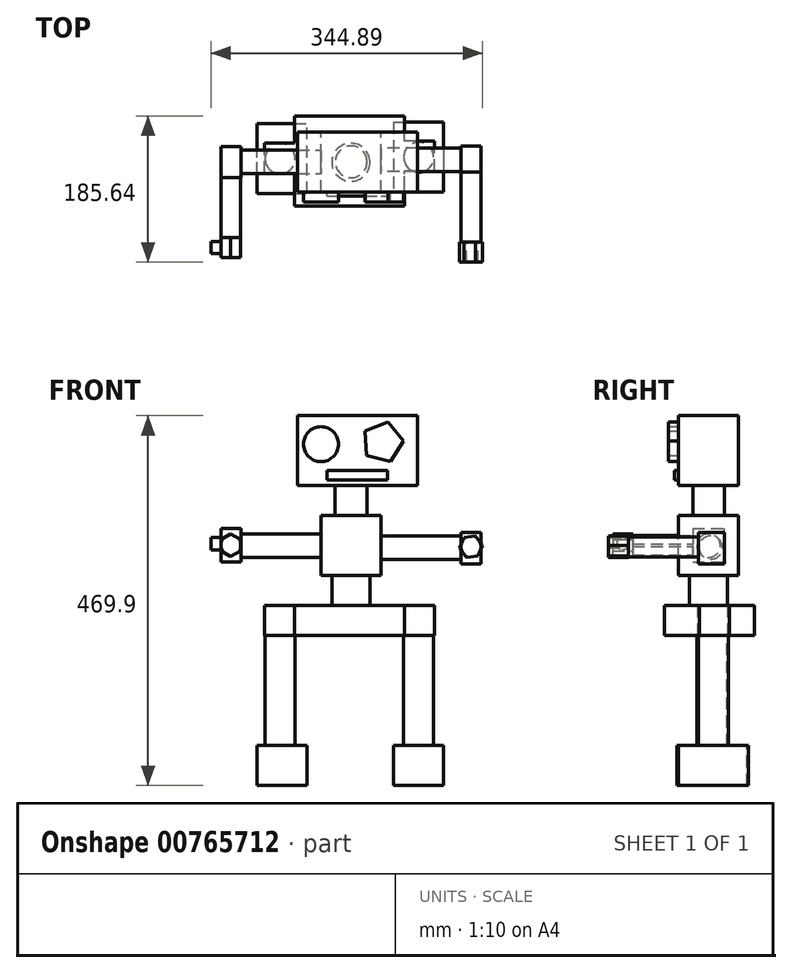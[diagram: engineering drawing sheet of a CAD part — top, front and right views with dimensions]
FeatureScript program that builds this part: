
annotation { "Feature Type Name" : "Feature", "Feature Type Description" : "" }
export const myFeature = defineFeature(function(context is Context, id is Id, definition is map)
    precondition{}
    {
        {
            var Q0;
            Q0=qCreatedBy(makeId("Front.planeOp"),FACE);
            var sketch = newSketch(context, id + "F0", { "sketchPlane" : qUnion([Q0])});
            skLineSegment(sketch, "E0.bottom", {"start": v(0, 0) * mm, "end": v(76.2, 0) * mm});
            skLineSegment(sketch, "E0.top", {"start": v(0, 76.2) * mm, "end": v(76.2, 76.2) * mm});
            skLineSegment(sketch, "E0.left", {"start": v(0, 0) * mm, "end": v(0, 76.2) * mm});
            skLineSegment(sketch, "E0.right", {"start": v(76.2, 0) * mm, "end": v(76.2, 76.2) * mm});
            skSolve(sketch);
        }
        {
            var Q0;
            Q0=makeQuery(id+"F0.imprint","IMPRINT",FACE,{"disambiguationData":[TD([[makeQuery(id+"F0.imprint","IMPRINT",EDGE,{"derivedFrom":sQuery(id+"F0.wireOp",EDGE,"E0.bottom")}),1.0]])]});
            extrude(context, id + "F1", {"entities" : qUnion([Q0]), "depth" : 76.2 * mm, "offsetDistance" : 25.4 * mm});
        }
        {
            var Q0;
            Q0=makeQuery(id+"F1.opExtrude","SWEPT_FACE",FACE,{"disambiguationData":[OSD([sQuery(id+"F0.wireOp",EDGE,"E0.bottom")])]});
            var sketch = newSketch(context, id + "F2", { "sketchPlane" : qUnion([Q0])});
            skPoint(sketch, "E1", {"position": v(38.1, 38.1) * mm});
            skSolve(sketch);
        }
        {
            var Q0;
            Q0=makeQuery(id+"F1.opExtrude","SWEPT_FACE",FACE,{"disambiguationData":[OSD([sQuery(id+"F0.wireOp",EDGE,"E0.right")])]});
            var sketch = newSketch(context, id + "F3", { "sketchPlane" : qUnion([Q0])});
            skCircle(sketch, "E2", {"center": v(-35.37, 35.61) * mm, "radius": 14.83 * mm});
            skSolve(sketch);
        }
        {
            var Q0;
            Q0 = qSketchRegion(id + "F3", true);
            extrude(context, id + "F4", {"entities" : qUnion([Q0]), "operationType" : NewBodyOperationType.ADD, "depth" : 101.6 * mm, "offsetDistance" : 25.4 * mm});
        }
        {
            var Q0;
            Q0=makeQuery(id+"F4.opExtrude","CAP_FACE",FACE,{"disambiguationData":[OSD([sQuery(id+"F3.wireOp",EDGE,"E2")])],"isStart":false});
            var sketch = newSketch(context, id + "F5", { "sketchPlane" : qUnion([Q0])});
            skLineSegment(sketch, "E3.bottom", {"start": v(-18.2, 54.98) * mm, "end": v(-51.02, 54.98) * mm});
            skLineSegment(sketch, "E3.top", {"start": v(-18.2, 14.56) * mm, "end": v(-51.02, 14.56) * mm});
            skLineSegment(sketch, "E3.left", {"start": v(-18.2, 54.98) * mm, "end": v(-18.2, 14.56) * mm});
            skLineSegment(sketch, "E3.right", {"start": v(-51.02, 54.98) * mm, "end": v(-51.02, 14.56) * mm});
            skSolve(sketch);
        }
        {
            var Q0;
            Q0 = qSketchRegion(id + "F5", true);
            extrude(context, id + "F6", {"entities" : qUnion([Q0]), "operationType" : NewBodyOperationType.ADD, "depth" : 25.4 * mm, "offsetDistance" : 25.4 * mm});
        }
        {
            var Q0;
            Q0=makeQuery(id+"F6.opExtrude","SWEPT_FACE",FACE,{"disambiguationData":[OSD([sQuery(id+"F5.wireOp",EDGE,"E3.right")])]});
            var sketch = newSketch(context, id + "F7", { "sketchPlane" : qUnion([Q0])});
            skCircle(sketch, "E4", {"center": v(190.5, 36.6) * mm, "radius": 12.7 * mm});
            skPoint(sketch, "E4.centerSnap0", {"position": v(190.5, 14.56) * mm});
            skSolve(sketch);
        }
        {
            var Q0;
            Q0 = qSketchRegion(id + "F7", true);
            extrude(context, id + "F8", {"entities" : qUnion([Q0]), "operationType" : NewBodyOperationType.ADD, "depth" : 88.9 * mm, "offsetDistance" : 25.4 * mm});
        }
        {
            var Q0;
            Q0=makeQuery(id+"F1.opExtrude","SWEPT_FACE",FACE,{"disambiguationData":[OSD([sQuery(id+"F0.wireOp",EDGE,"E0.left")])]});
            var sketch = newSketch(context, id + "F9", { "sketchPlane" : qUnion([Q0])});
            skPoint(sketch, "E5", {"position": v(38.1, 38.1) * mm});
            skPoint(sketch, "E5.positionSnap0", {"position": v(0, 38.1) * mm});
            skSolve(sketch);
        }
        {
            var Q0;
            {var subQ0=sQuery(id+"F0.wireOp",EDGE,"E0.left");Q0=makeQuery(id+"F9.imprint","IMPRINT",FACE,{"disambiguationData":[TD([[makeQuery(id+"F9.imprint","IMPRINT",EDGE,{"derivedFrom":makeQuery(id+"F1.opExtrude","CAP_EDGE",EDGE,{"disambiguationData":[OSD([subQ0])],"isStart":true})}),-1.0]])]});}
            var sketch = newSketch(context, id + "F10", { "sketchPlane" : qUnion([Q0])});
            skCircle(sketch, "E6", {"center": v(38.01, 38.14) * mm, "radius": 14.96 * mm});
            skSolve(sketch);
        }
        {
            var Q0;
            Q0 = qSketchRegion(id + "F10", true);
            extrude(context, id + "F11", {"entities" : qUnion([Q0]), "operationType" : NewBodyOperationType.ADD, "depth" : 101.6 * mm, "offsetDistance" : 25.4 * mm});
        }
        {
            var Q0;
            Q0=makeQuery(id+"F11.opExtrude","CAP_FACE",FACE,{"disambiguationData":[OSD([sQuery(id+"F10.wireOp",EDGE,"E6")])],"isStart":false});
            var sketch = newSketch(context, id + "F12", { "sketchPlane" : qUnion([Q0])});
            skLineSegment(sketch, "E7.bottom", {"start": v(58.05, 59.82) * mm, "end": v(18.68, 59.82) * mm});
            skLineSegment(sketch, "E7.top", {"start": v(58.05, 17.57) * mm, "end": v(18.68, 17.57) * mm});
            skLineSegment(sketch, "E7.left", {"start": v(58.05, 59.82) * mm, "end": v(58.05, 17.57) * mm});
            skLineSegment(sketch, "E7.right", {"start": v(18.68, 59.82) * mm, "end": v(18.68, 17.57) * mm});
            skSolve(sketch);
        }
        {
            var Q0;
            Q0 = qSketchRegion(id + "F12", true);
            extrude(context, id + "F13", {"entities" : qUnion([Q0]), "operationType" : NewBodyOperationType.ADD, "depth" : 25.4 * mm, "offsetDistance" : 25.4 * mm});
        }
        {
            var Q0;
            Q0=makeQuery(id+"F13.opExtrude","SWEPT_FACE",FACE,{"disambiguationData":[OSD([sQuery(id+"F12.wireOp",EDGE,"E7.left")])]});
            var sketch = newSketch(context, id + "F14", { "sketchPlane" : qUnion([Q0])});
            skCircle(sketch, "E8", {"center": v(-114.67, 38.58) * mm, "radius": 12.46 * mm});
            skSolve(sketch);
        }
        {
            var Q0;
            {var subQ0=sQuery(id+"F14.wireOp",EDGE,"E8");var subQ1=makeQuery(id+"F13.opExtrude","CAP_EDGE",EDGE,{"disambiguationData":[OSD([sQuery(id+"F12.wireOp",EDGE,"E7.left")])],"isStart":false});var subQ2=makeQuery(id+"F14.imprint","INTERSECT",VERTEX,{"disambiguationData":[OD(0.0)],"derivedFrom":[subQ1,subQ0]});Q0=makeQuery(id+"F14.imprint","IMPRINT",FACE,{"disambiguationData":[TD([[makeQuery(id+"F14.imprint","IMPRINT",EDGE,{"disambiguationData":[TD([[subQ2,1.0]])],"derivedFrom":subQ0}),1.0]])]});}
            extrude(context, id + "F15", {"entities" : qUnion([Q0]), "operationType" : NewBodyOperationType.ADD, "depth" : 76.2 * mm, "offsetDistance" : 25.4 * mm});
        }
        {
            var Q0;
            Q0=makeQuery(id+"F15.opExtrude","CAP_FACE",FACE,{"disambiguationData":[OSD([sQuery(id+"F14.wireOp",EDGE,"E8")])],"isStart":false});
            var sketch = newSketch(context, id + "F16", { "sketchPlane" : qUnion([Q0])});
            skCircle(sketch, "E9.cCircle", {"center": v(-114.67, 38.58) * mm, "radius": 12.46 * mm, "construction": true});
            skLineSegment(sketch, "E9.0", {"start": v(-102.2, 45.77) * mm, "end": v(-102.2, 31.38) * mm});
            skLineSegment(sketch, "E9.1", {"start": v(-102.2, 31.38) * mm, "end": v(-114.67, 24.18) * mm});
            skLineSegment(sketch, "E9.2", {"start": v(-114.67, 24.18) * mm, "end": v(-127.13, 31.38) * mm});
            skLineSegment(sketch, "E9.3", {"start": v(-127.13, 31.38) * mm, "end": v(-127.13, 45.77) * mm});
            skLineSegment(sketch, "E9.4", {"start": v(-127.13, 45.77) * mm, "end": v(-114.67, 52.97) * mm});
            skLineSegment(sketch, "E9.5", {"start": v(-114.67, 52.97) * mm, "end": v(-102.2, 45.77) * mm});
            skPoint(sketch, "E9.0.midPoint", {"position": v(-102.2, 38.58) * mm});
            skSolve(sketch);
        }
        {
            var Q0;
            Q0 = qSketchRegion(id + "F16", true);
            extrude(context, id + "F17", {"entities" : qUnion([Q0]), "operationType" : NewBodyOperationType.ADD, "depth" : 25.4 * mm, "offsetDistance" : 25.4 * mm});
        }
        {
            var Q0;
            Q0=makeQuery(id+"F8.opExtrude","CAP_FACE",FACE,{"disambiguationData":[OSD([sQuery(id+"F7.wireOp",EDGE,"E4")])],"isStart":false});
            var sketch = newSketch(context, id + "F18", { "sketchPlane" : qUnion([Q0])});
            skCircle(sketch, "E10.cCircle", {"center": v(190.5, 36.6) * mm, "radius": 12.7 * mm, "construction": true});
            skLineSegment(sketch, "E10.0", {"start": v(205.06, 38.37) * mm, "end": v(199.31, 24.88) * mm});
            skLineSegment(sketch, "E10.1", {"start": v(199.31, 24.88) * mm, "end": v(184.75, 23.11) * mm});
            skLineSegment(sketch, "E10.2", {"start": v(184.75, 23.11) * mm, "end": v(175.94, 34.83) * mm});
            skLineSegment(sketch, "E10.3", {"start": v(175.94, 34.83) * mm, "end": v(181.69, 48.33) * mm});
            skLineSegment(sketch, "E10.4", {"start": v(181.69, 48.33) * mm, "end": v(196.25, 50.1) * mm});
            skLineSegment(sketch, "E10.5", {"start": v(196.25, 50.1) * mm, "end": v(205.06, 38.37) * mm});
            skPoint(sketch, "E10.0.midPoint", {"position": v(202.18, 31.63) * mm});
            skSolve(sketch);
        }
        {
            var Q0;
            Q0 = qSketchRegion(id + "F18", true);
            extrude(context, id + "F19", {"entities" : qUnion([Q0]), "operationType" : NewBodyOperationType.ADD, "depth" : 25.4 * mm, "offsetDistance" : 25.4 * mm});
        }
        {
            var Q0;
            {var subQ0=sQuery(id+"F0.wireOp",EDGE,"E0.bottom");Q0=makeQuery(id+"F2.imprint","IMPRINT",FACE,{"disambiguationData":[TD([[makeQuery(id+"F2.imprint","IMPRINT",EDGE,{"derivedFrom":makeQuery(id+"F1.opExtrude","CAP_EDGE",EDGE,{"disambiguationData":[OSD([subQ0])],"isStart":true})}),1.0]])]});}
            var sketch = newSketch(context, id + "F20", { "sketchPlane" : qUnion([Q0])});
            skCircle(sketch, "E11", {"center": v(37.98, 38.47) * mm, "radius": 24.15 * mm});
            skSolve(sketch);
        }
        {
            var Q0;
            Q0 = qSketchRegion(id + "F20", true);
            extrude(context, id + "F21", {"entities" : qUnion([Q0]), "operationType" : NewBodyOperationType.ADD, "depth" : 38.1 * mm, "offsetDistance" : 25.4 * mm});
        }
        {
            var Q0;
            Q0=makeQuery(id+"F21.opExtrude","CAP_FACE",FACE,{"disambiguationData":[OSD([sQuery(id+"F20.wireOp",EDGE,"E11")])],"isStart":false});
            var sketch = newSketch(context, id + "F22", { "sketchPlane" : qUnion([Q0])});
            skLineSegment(sketch, "E12.bottom", {"start": v(-33.76, 93.98) * mm, "end": v(105.94, 93.98) * mm});
            skLineSegment(sketch, "E12.top", {"start": v(-33.76, -20.32) * mm, "end": v(105.94, -20.32) * mm});
            skLineSegment(sketch, "E12.left", {"start": v(-33.76, 93.98) * mm, "end": v(-33.76, -20.32) * mm});
            skLineSegment(sketch, "E12.right", {"start": v(105.94, 93.98) * mm, "end": v(105.94, -20.32) * mm});
            skSolve(sketch);
        }
        {
            var Q0;
            Q0 = qSketchRegion(id + "F22", true);
            extrude(context, id + "F23", {"entities" : qUnion([Q0]), "operationType" : NewBodyOperationType.ADD, "depth" : 38.1 * mm, "offsetDistance" : 25.4 * mm});
        }
        {
            var Q0;
            Q0=makeQuery(id+"F23.opExtrude","SWEPT_FACE",FACE,{"disambiguationData":[OSD([sQuery(id+"F22.wireOp",EDGE,"E12.right")])]});
            var sketch = newSketch(context, id + "F24", { "sketchPlane" : qUnion([Q0])});
            skLineSegment(sketch, "E13.bottom", {"start": v(-49.7, -76.2) * mm, "end": v(-11.6, -76.2) * mm});
            skLineSegment(sketch, "E13.top", {"start": v(-49.7, -38.1) * mm, "end": v(-11.6, -38.1) * mm});
            skLineSegment(sketch, "E13.left", {"start": v(-49.7, -76.2) * mm, "end": v(-49.7, -38.1) * mm});
            skLineSegment(sketch, "E13.right", {"start": v(-11.6, -76.2) * mm, "end": v(-11.6, -38.1) * mm});
            skSolve(sketch);
        }
        {
            var Q0;
            Q0 = qSketchRegion(id + "F24", true);
            extrude(context, id + "F25", {"entities" : qUnion([Q0]), "operationType" : NewBodyOperationType.ADD, "depth" : 38.1 * mm, "offsetDistance" : 25.4 * mm});
        }
        {
            var Q0;
            Q0=makeQuery(id+"F23.opExtrude","SWEPT_FACE",FACE,{"disambiguationData":[OSD([sQuery(id+"F22.wireOp",EDGE,"E12.left")])]});
            var sketch = newSketch(context, id + "F26", { "sketchPlane" : qUnion([Q0])});
            skLineSegment(sketch, "E14.bottom", {"start": v(14.15, -38.1) * mm, "end": v(52.25, -38.1) * mm});
            skLineSegment(sketch, "E14.top", {"start": v(14.15, -76.2) * mm, "end": v(52.25, -76.2) * mm});
            skLineSegment(sketch, "E14.left", {"start": v(14.15, -38.1) * mm, "end": v(14.15, -76.2) * mm});
            skLineSegment(sketch, "E14.right", {"start": v(52.25, -38.1) * mm, "end": v(52.25, -76.2) * mm});
            skSolve(sketch);
        }
        {
            var Q0;
            Q0 = qSketchRegion(id + "F26", true);
            extrude(context, id + "F27", {"entities" : qUnion([Q0]), "operationType" : NewBodyOperationType.ADD, "depth" : 38.1 * mm, "offsetDistance" : 25.4 * mm});
        }
        {
            var Q0;
            Q0=makeQuery(id+"F27.boolean.opBoolean","MERGE",FACE,{"derivedFrom":[makeQuery(id+"F25.boolean.opBoolean","MERGE",FACE,{"derivedFrom":[makeQuery(id+"F23.opExtrude","CAP_FACE",FACE,{"disambiguationData":[OSD([sQuery(id+"F22.wireOp",EDGE,"E12.bottom"),sQuery(id+"F22.wireOp",EDGE,"E12.top"),sQuery(id+"F22.wireOp",EDGE,"E12.left"),sQuery(id+"F22.wireOp",EDGE,"E12.right")])],"isStart":false}),makeQuery(id+"F25.opExtrude","SWEPT_FACE",FACE,{"disambiguationData":[OSD([sQuery(id+"F24.wireOp",EDGE,"E13.bottom")])]})]}),makeQuery(id+"F27.opExtrude","SWEPT_FACE",FACE,{"disambiguationData":[OSD([sQuery(id+"F26.wireOp",EDGE,"E14.top")])]})]});
            var sketch = newSketch(context, id + "F28", { "sketchPlane" : qUnion([Q0])});
            skCircle(sketch, "E15", {"center": v(124.16, 32.01) * mm, "radius": 19.05 * mm});
            skSolve(sketch);
        }
        {
            var Q0;
            Q0 = qSketchRegion(id + "F28", true);
            extrude(context, id + "F29", {"entities" : qUnion([Q0]), "operationType" : NewBodyOperationType.ADD, "depth" : 139.7 * mm, "offsetDistance" : 25.4 * mm});
        }
        {
            var Q0;
            Q0=makeQuery(id+"F27.boolean.opBoolean","MERGE",FACE,{"derivedFrom":[makeQuery(id+"F25.boolean.opBoolean","MERGE",FACE,{"derivedFrom":[makeQuery(id+"F23.opExtrude","CAP_FACE",FACE,{"disambiguationData":[OSD([sQuery(id+"F22.wireOp",EDGE,"E12.bottom"),sQuery(id+"F22.wireOp",EDGE,"E12.top"),sQuery(id+"F22.wireOp",EDGE,"E12.left"),sQuery(id+"F22.wireOp",EDGE,"E12.right")])],"isStart":false}),makeQuery(id+"F25.opExtrude","SWEPT_FACE",FACE,{"disambiguationData":[OSD([sQuery(id+"F24.wireOp",EDGE,"E13.bottom")])]})]}),makeQuery(id+"F27.opExtrude","SWEPT_FACE",FACE,{"disambiguationData":[OSD([sQuery(id+"F26.wireOp",EDGE,"E14.top")])]})]});
            var sketch = newSketch(context, id + "F30", { "sketchPlane" : qUnion([Q0])});
            skCircle(sketch, "E16", {"center": v(-51.92, 33.94) * mm, "radius": 19.05 * mm});
            skSolve(sketch);
        }
        {
            var Q0;
            Q0 = qSketchRegion(id + "F30", true);
            extrude(context, id + "F31", {"entities" : qUnion([Q0]), "operationType" : NewBodyOperationType.ADD, "depth" : 139.7 * mm, "offsetDistance" : 25.4 * mm});
        }
        {
            var Q0;
            Q0=makeQuery(id+"F31.opExtrude","CAP_FACE",FACE,{"disambiguationData":[OSD([sQuery(id+"F30.wireOp",EDGE,"E16")])],"isStart":false});
            var sketch = newSketch(context, id + "F32", { "sketchPlane" : qUnion([Q0])});
            skLineSegment(sketch, "E17.bottom", {"start": v(-81.3, 78.25) * mm, "end": v(-17.8, 78.25) * mm});
            skLineSegment(sketch, "E17.top", {"start": v(-81.3, -10.65) * mm, "end": v(-17.8, -10.65) * mm});
            skLineSegment(sketch, "E17.left", {"start": v(-81.3, 78.25) * mm, "end": v(-81.3, -10.65) * mm});
            skLineSegment(sketch, "E17.right", {"start": v(-17.8, 78.25) * mm, "end": v(-17.8, -10.65) * mm});
            skSolve(sketch);
        }
        {
            var Q0;
            Q0 = qSketchRegion(id + "F32", true);
            extrude(context, id + "F33", {"entities" : qUnion([Q0]), "operationType" : NewBodyOperationType.ADD, "depth" : 50.8 * mm, "offsetDistance" : 25.4 * mm});
        }
        {
            var Q0;
            Q0=makeQuery(id+"F29.opExtrude","CAP_FACE",FACE,{"disambiguationData":[OSD([sQuery(id+"F28.wireOp",EDGE,"E15")])],"isStart":false});
            var sketch = newSketch(context, id + "F34", { "sketchPlane" : qUnion([Q0])});
            skLineSegment(sketch, "E18.bottom", {"start": v(92.4, -12.44) * mm, "end": v(155.9, -12.44) * mm});
            skLineSegment(sketch, "E18.top", {"start": v(92.4, 76.46) * mm, "end": v(155.9, 76.46) * mm});
            skLineSegment(sketch, "E18.left", {"start": v(92.4, -12.44) * mm, "end": v(92.4, 76.46) * mm});
            skLineSegment(sketch, "E18.right", {"start": v(155.9, -12.44) * mm, "end": v(155.9, 76.46) * mm});
            skPoint(sketch, "E18.middle", {"position": v(124.16, 32.01) * mm});
            skSolve(sketch);
        }
        {
            var Q0;
            Q0 = qSketchRegion(id + "F34", true);
            extrude(context, id + "F35", {"entities" : qUnion([Q0]), "operationType" : NewBodyOperationType.ADD, "depth" : 50.8 * mm, "offsetDistance" : 25.4 * mm});
        }
        {
            var Q0;
            Q0=makeQuery(id+"F1.opExtrude","SWEPT_FACE",FACE,{"disambiguationData":[OSD([sQuery(id+"F0.wireOp",EDGE,"E0.top")])]});
            var sketch = newSketch(context, id + "F36", { "sketchPlane" : qUnion([Q0])});
            skPoint(sketch, "E19", {"position": v(38.3, -37.84) * mm});
            skCircle(sketch, "E20", {"center": v(38.3, -37.84) * mm, "radius": 20.2 * mm});
            skSolve(sketch);
        }
        {
            var Q0;
            Q0 = qSketchRegion(id + "F36", true);
            extrude(context, id + "F37", {"entities" : qUnion([Q0]), "operationType" : NewBodyOperationType.ADD, "depth" : 38.1 * mm, "offsetDistance" : 25.4 * mm});
        }
        {
            var Q0;
            Q0=makeQuery(id+"F37.opExtrude","CAP_FACE",FACE,{"disambiguationData":[OSD([sQuery(id+"F36.wireOp",EDGE,"E20")])],"isStart":false});
            var sketch = newSketch(context, id + "F38", { "sketchPlane" : qUnion([Q0])});
            skLineSegment(sketch, "E21.bottom", {"start": v(-29.87, 0) * mm, "end": v(122.53, 0) * mm});
            skLineSegment(sketch, "E21.top", {"start": v(-29.87, -76.2) * mm, "end": v(122.53, -76.2) * mm});
            skLineSegment(sketch, "E21.left", {"start": v(-29.87, 0) * mm, "end": v(-29.87, -76.2) * mm});
            skLineSegment(sketch, "E21.right", {"start": v(122.53, 0) * mm, "end": v(122.53, -76.2) * mm});
            skSolve(sketch);
        }
        {
            var Q0;
            Q0 = qSketchRegion(id + "F38", true);
            extrude(context, id + "F39", {"entities" : qUnion([Q0]), "operationType" : NewBodyOperationType.ADD, "depth" : 88.9 * mm, "offsetDistance" : 25.4 * mm});
        }
        {
            var Q0;
            Q0=makeQuery(id+"F39.opExtrude","SWEPT_FACE",FACE,{"disambiguationData":[OSD([sQuery(id+"F38.wireOp",EDGE,"E21.top")])]});
            var sketch = newSketch(context, id + "F40", { "sketchPlane" : qUnion([Q0])});
            skCircle(sketch, "E22", {"center": v(0, 166.89) * mm, "radius": 22.2 * mm});
            skSolve(sketch);
        }
        {
            var Q0;
            Q0 = qSketchRegion(id + "F40", true);
            extrude(context, id + "F41", {"entities" : qUnion([Q0]), "operationType" : NewBodyOperationType.ADD, "depth" : 12.7 * mm, "offsetDistance" : 25.4 * mm});
        }
        {
            var Q0;
            Q0=makeQuery(id+"F39.opExtrude","SWEPT_FACE",FACE,{"disambiguationData":[OSD([sQuery(id+"F38.wireOp",EDGE,"E21.top")])]});
            var sketch = newSketch(context, id + "F42", { "sketchPlane" : qUnion([Q0])});
            skCircle(sketch, "E23.cCircle", {"center": v(78.32, 169.57) * mm, "radius": 21.37 * mm, "construction": true});
            skLineSegment(sketch, "E23.0", {"start": v(104.68, 171.27) * mm, "end": v(88.08, 145.02) * mm});
            skLineSegment(sketch, "E23.1", {"start": v(88.08, 145.02) * mm, "end": v(57.98, 152.7) * mm});
            skLineSegment(sketch, "E23.2", {"start": v(57.98, 152.7) * mm, "end": v(55.99, 183.7) * mm});
            skLineSegment(sketch, "E23.3", {"start": v(55.99, 183.7) * mm, "end": v(84.85, 195.17) * mm});
            skLineSegment(sketch, "E23.4", {"start": v(84.85, 195.17) * mm, "end": v(104.68, 171.27) * mm});
            skPoint(sketch, "E23.0.midPoint", {"position": v(96.38, 158.15) * mm});
            skSolve(sketch);
        }
        {
            var Q0;
            Q0 = qSketchRegion(id + "F42", true);
            extrude(context, id + "F43", {"entities" : qUnion([Q0]), "operationType" : NewBodyOperationType.ADD, "depth" : 12.7 * mm, "offsetDistance" : 25.4 * mm});
        }
        {
            var Q0;
            Q0=makeQuery(id+"F17.opExtrude","SWEPT_FACE",FACE,{"disambiguationData":[OSD([sQuery(id+"F16.wireOp",EDGE,"E9.3")])]});
            var sketch = newSketch(context, id + "F44", { "sketchPlane" : qUnion([Q0])});
            skCircle(sketch, "E24", {"center": v(146.95, 40.6) * mm, "radius": 7.75 * mm});
            skPoint(sketch, "E24.centerSnap0", {"position": v(146.95, 31.38) * mm});
            skSolve(sketch);
        }
        {
            var Q0;
            Q0 = qSketchRegion(id + "F44", true);
            extrude(context, id + "F45", {"entities" : qUnion([Q0]), "operationType" : NewBodyOperationType.ADD, "depth" : 12.7 * mm, "offsetDistance" : 25.4 * mm});
        }
        {
            var Q0;
            Q0=makeQuery(id+"F39.opExtrude","SWEPT_FACE",FACE,{"disambiguationData":[OSD([sQuery(id+"F38.wireOp",EDGE,"E21.top")])]});
            var sketch = newSketch(context, id + "F46", { "sketchPlane" : qUnion([Q0])});
            skLineSegment(sketch, "E25.bottom", {"start": v(7.43, 133.67) * mm, "end": v(84.57, 133.67) * mm});
            skLineSegment(sketch, "E25.top", {"start": v(7.43, 121.56) * mm, "end": v(84.57, 121.56) * mm});
            skLineSegment(sketch, "E25.left", {"start": v(7.43, 133.67) * mm, "end": v(7.43, 121.56) * mm});
            skLineSegment(sketch, "E25.right", {"start": v(84.57, 133.67) * mm, "end": v(84.57, 121.56) * mm});
            skSolve(sketch);
        }
        {
            var Q0;
            Q0 = qSketchRegion(id + "F46", true);
            extrude(context, id + "F47", {"entities" : qUnion([Q0]), "operationType" : NewBodyOperationType.ADD, "depth" : 5.08 * mm, "offsetDistance" : 25.4 * mm});
        }
    });
